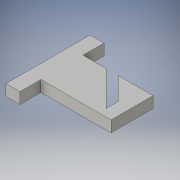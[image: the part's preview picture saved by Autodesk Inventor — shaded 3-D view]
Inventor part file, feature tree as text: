
AUTODESK INVENTOR PART (.ipt)
format: ipt  version: 2016 (Build 200138000, 138)  size: 96,256 bytes
history: native  units: in
note: dims shown in document units (in); Inventor stores cm internally (conversion verified against a paired STEP export)
features: sketch x2, extrude x1
ambient origin geometry x8: Origin, YZ Plane, XZ Plane, XY Plane, X Axis, Y Axis, Z Axis, Center Point
bodies: Solid1 (feature_tree)
feature tree (3):
  sketch  "Sketch1"  dims[d7=0.315in d8=0.0in]
  sketch  "Sketch2"
  extrude  "Extrusion1"  [1 undecoded]
note: 1 required parameter value undecoded (feature->parameter linkage not recoverable at this tier; creation-order binding heuristic only, values carry confidence <= 0.55)
